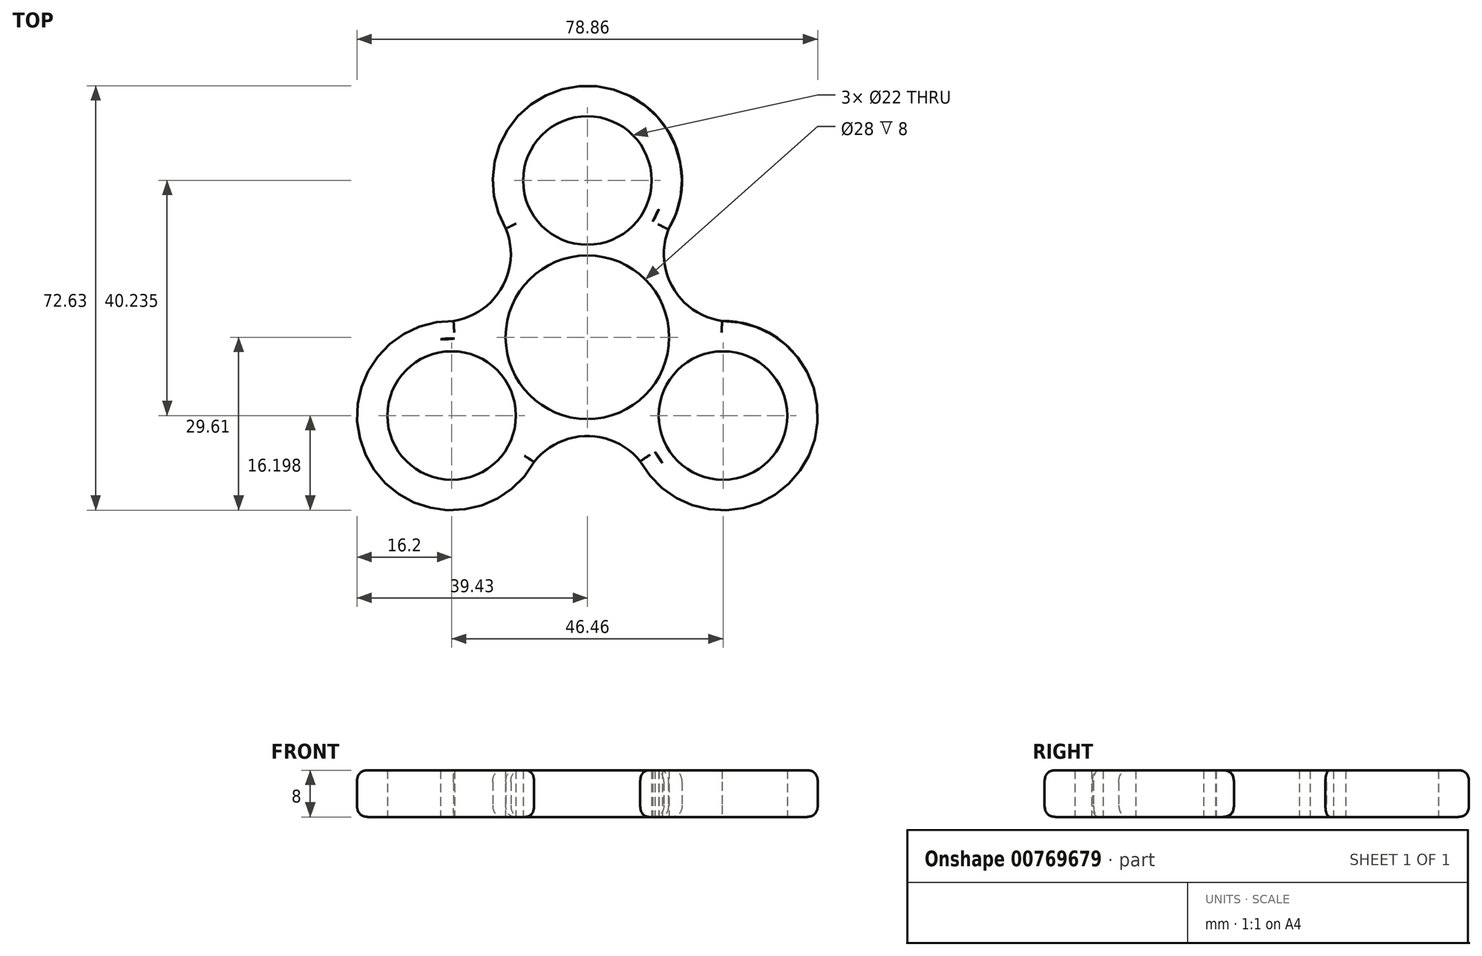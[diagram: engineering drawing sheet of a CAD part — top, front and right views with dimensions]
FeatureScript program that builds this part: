
annotation { "Feature Type Name" : "Feature", "Feature Type Description" : "" }
export const myFeature = defineFeature(function(context is Context, id is Id, definition is map)
    precondition{}
    {
        {
            var Q0;
            Q0=qCreatedBy(makeId("Top.planeOp"),FACE);
            var sketch = newSketch(context, id + "F0", { "sketchPlane" : qUnion([Q0])});
            skCircle(sketch, "E0", {"center": v(0, 0) * mm, "radius": 14 * mm});
            skCircle(sketch, "E1", {"center": v(0, 26.82) * mm, "radius": 11 * mm});
            skArc(sketch, "E2", {"start": v(11.18, 19.8) * mm, "mid": v(0.09, 40.02) * mm, "end": v(-11.27, 19.95) * mm});
            skArc(sketch, "E3.1.0", {"start": v(-22.74, -0.22) * mm, "mid": v(-34.7, -19.94) * mm, "end": v(-11.64, -19.73) * mm});
            skCircle(sketch, "E3.1.1", {"center": v(-23.23, -13.41) * mm, "radius": 11 * mm});
            skArc(sketch, "E3.2.0", {"start": v(11.56, -19.58) * mm, "mid": v(34.62, -20.09) * mm, "end": v(22.9, -0.22) * mm});
            skCircle(sketch, "E3.2.1", {"center": v(23.23, -13.41) * mm, "radius": 11 * mm});
            skArc(sketch, "E4", {"start": v(12.26, 21.92) * mm, "mid": v(11.53, 7.94) * mm, "end": v(22.9, -0.22) * mm});
            skArc(sketch, "E5.1.0", {"start": v(-25.11, -0.35) * mm, "mid": v(-12.64, 6.01) * mm, "end": v(-11.27, 19.95) * mm});
            skArc(sketch, "E5.2.0", {"start": v(12.86, -21.58) * mm, "mid": v(1.11, -13.96) * mm, "end": v(-11.64, -19.73) * mm});
            skArc(sketch, "E6.0", {"start": v(-22.62, 2.78) * mm, "mid": v(-37.31, -21.42) * mm, "end": v(-9, -21.17) * mm});
            skArc(sketch, "E7.0", {"start": v(-25.03, 2.65) * mm, "mid": v(-15.12, 7.7) * mm, "end": v(-14.03, 18.77) * mm});
            skArc(sketch, "E8.0", {"start": v(13.72, 18.2) * mm, "mid": v(0.1, 43.02) * mm, "end": v(-13.83, 18.38) * mm});
            skArc(sketch, "E9.0", {"start": v(14.81, 20.35) * mm, "mid": v(14.23, 9.24) * mm, "end": v(23.27, 2.76) * mm});
            skArc(sketch, "E10.0", {"start": v(8.9, -20.98) * mm, "mid": v(37.2, -21.6) * mm, "end": v(22.83, 2.78) * mm});
            skArc(sketch, "E11.0", {"start": v(10.22, -23) * mm, "mid": v(0.89, -16.95) * mm, "end": v(-9.24, -21.53) * mm});
            skSolve(sketch);
        }
        {
            var Q0;
            Q0=makeQuery(id+"F0.imprint","IMPRINT",FACE,{"disambiguationData":[TD([[makeQuery(id+"F0.imprint","IMPRINT",EDGE,{"derivedFrom":sQuery(id+"F0.wireOp",EDGE,"E0")}),-1.0]])]});
            var Q1;
            {var subQ0=sQuery(id+"F0.wireOp",EDGE,"E4");var subQ1=sQuery(id+"F0.wireOp",EDGE,"E2");var subQ2=makeQuery(id+"F0.imprint","INTERSECT",VERTEX,{"disambiguationData":[OD(0.0)],"derivedFrom":[subQ1,subQ0]});Q1=makeQuery(id+"F0.imprint","IMPRINT",FACE,{"disambiguationData":[TD([[makeQuery(id+"F0.imprint","IMPRINT",EDGE,{"disambiguationData":[TD([[subQ2,-1.0]])],"derivedFrom":subQ1}),-1.0]])]});}
            var Q2;
            Q2=makeQuery(id+"F0.imprint","IMPRINT",FACE,{"disambiguationData":[TD([[makeQuery(id+"F0.imprint","IMPRINT",EDGE,{"derivedFrom":sQuery(id+"F0.wireOp",EDGE,"E1")}),-1.0]])]});
            var Q3;
            Q3=makeQuery(id+"F0.imprint","IMPRINT",FACE,{"disambiguationData":[TD([[makeQuery(id+"F0.imprint","IMPRINT",EDGE,{"derivedFrom":sQuery(id+"F0.wireOp",EDGE,"E3.1.1")}),-1.0]])]});
            var Q4;
            Q4=makeQuery(id+"F0.imprint","IMPRINT",FACE,{"disambiguationData":[TD([[makeQuery(id+"F0.imprint","IMPRINT",EDGE,{"derivedFrom":sQuery(id+"F0.wireOp",EDGE,"E3.2.1")}),-1.0]])]});
            extrude(context, id + "F1", {"entities" : qUnion([Q0, Q1, Q2, Q3, Q4]), "endBound" : BoundingType.SYMMETRIC, "depth" : 8 * mm, "offsetDistance" : 25 * mm});
        }
        {
            var Q0;
            Q0=makeQuery(id+"F1.opExtrude","CAP_EDGE",EDGE,{"disambiguationData":[OSD([sQuery(id+"F0.wireOp",EDGE,"E7.0")])],"isStart":false});
            var Q1;
            Q1=makeQuery(id+"F1.opExtrude","CAP_EDGE",EDGE,{"disambiguationData":[OSD([sQuery(id+"F0.wireOp",EDGE,"E11.0")])],"isStart":false});
            var Q2;
            Q2=makeQuery(id+"F1.opExtrude","CAP_EDGE",EDGE,{"disambiguationData":[OSD([sQuery(id+"F0.wireOp",EDGE,"E9.0")])],"isStart":false});
            var Q3;
            Q3=makeQuery(id+"F1.opExtrude","CAP_EDGE",EDGE,{"disambiguationData":[OSD([sQuery(id+"F0.wireOp",EDGE,"E8.0")])],"isStart":false});
            var Q4;
            Q4=makeQuery(id+"F1.opExtrude","CAP_EDGE",EDGE,{"disambiguationData":[OSD([sQuery(id+"F0.wireOp",EDGE,"E10.0")])],"isStart":false});
            var Q5;
            Q5=makeQuery(id+"F1.opExtrude","CAP_EDGE",EDGE,{"disambiguationData":[OSD([sQuery(id+"F0.wireOp",EDGE,"E6.0")])],"isStart":false});
            var Q6;
            Q6=makeQuery(id+"F1.opExtrude","CAP_EDGE",EDGE,{"disambiguationData":[OSD([sQuery(id+"F0.wireOp",EDGE,"E11.0")])],"isStart":true});
            var Q7;
            Q7=makeQuery(id+"F1.opExtrude","CAP_EDGE",EDGE,{"disambiguationData":[OSD([sQuery(id+"F0.wireOp",EDGE,"E7.0")])],"isStart":true});
            var Q8;
            Q8=makeQuery(id+"F1.opExtrude","CAP_EDGE",EDGE,{"disambiguationData":[OSD([sQuery(id+"F0.wireOp",EDGE,"E9.0")])],"isStart":true});
            var Q9;
            Q9=makeQuery(id+"F1.opExtrude","CAP_EDGE",EDGE,{"disambiguationData":[OSD([sQuery(id+"F0.wireOp",EDGE,"E10.0")])],"isStart":true});
            var Q10;
            Q10=makeQuery(id+"F1.opExtrude","CAP_EDGE",EDGE,{"disambiguationData":[OSD([sQuery(id+"F0.wireOp",EDGE,"E6.0")])],"isStart":true});
            var Q11;
            Q11=makeQuery(id+"F1.opExtrude","CAP_EDGE",EDGE,{"disambiguationData":[OSD([sQuery(id+"F0.wireOp",EDGE,"E8.0")])],"isStart":true});
            fillet(context, id + "F2", {"entities" : qUnion([Q0, Q1, Q2, Q3, Q4, Q5, Q6, Q7, Q8, Q9, Q10, Q11]), "radius" : 2 * mm, "tangentPropagation" : true, "rho" : 0.5, "crossSection" : FilletCrossSection.CONIC, "allowEdgeOverflow" : false});
        }
    });
